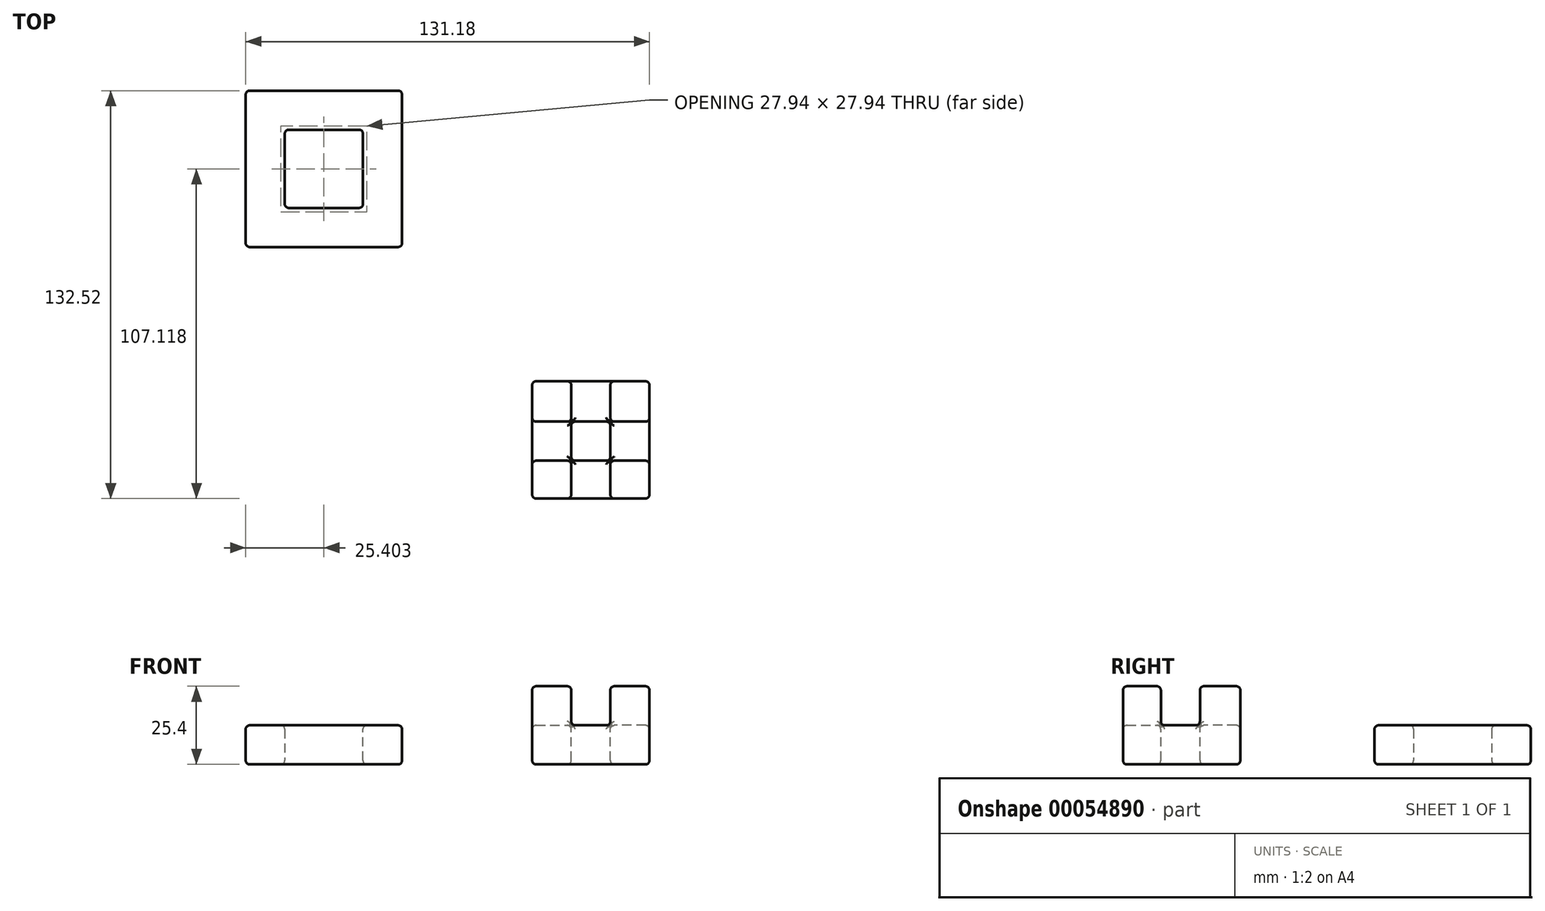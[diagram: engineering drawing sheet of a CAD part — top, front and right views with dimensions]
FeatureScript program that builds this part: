
annotation { "Feature Type Name" : "Feature", "Feature Type Description" : "" }
export const myFeature = defineFeature(function(context is Context, id is Id, definition is map)
    precondition{}
    {
        {
            var Q0;
            Q0=qCreatedBy(makeId("Top.planeOp"),FACE);
            var sketch = newSketch(context, id + "F0", { "sketchPlane" : qUnion([Q0])});
            skLineSegment(sketch, "E0.bottom", {"start": v(-78.93, 70.47) * mm, "end": v(-66.23, 70.47) * mm});
            skLineSegment(sketch, "E0.top", {"start": v(-78.93, 19.67) * mm, "end": v(-66.23, 19.67) * mm});
            skLineSegment(sketch, "E0.left", {"start": v(-78.93, 70.47) * mm, "end": v(-78.93, 19.67) * mm});
            skLineSegment(sketch, "E0.right", {"start": v(-66.23, 70.47) * mm, "end": v(-66.23, 19.67) * mm});
            skLineSegment(sketch, "E1.bottom", {"start": v(-78.93, 19.67) * mm, "end": v(-40.83, 19.67) * mm});
            skLineSegment(sketch, "E1.top", {"start": v(-78.93, 32.37) * mm, "end": v(-40.83, 32.37) * mm});
            skLineSegment(sketch, "E1.left", {"start": v(-78.93, 19.67) * mm, "end": v(-78.93, 32.37) * mm});
            skLineSegment(sketch, "E1.right", {"start": v(-40.83, 19.67) * mm, "end": v(-40.83, 32.37) * mm});
            skLineSegment(sketch, "E2.bottom", {"start": v(-28.13, 19.67) * mm, "end": v(-40.83, 19.67) * mm});
            skLineSegment(sketch, "E2.top", {"start": v(-28.13, 70.47) * mm, "end": v(-40.83, 70.47) * mm});
            skLineSegment(sketch, "E2.left", {"start": v(-40.83, 19.67) * mm, "end": v(-40.83, 70.47) * mm});
            skLineSegment(sketch, "E2.right", {"start": v(-28.13, 19.67) * mm, "end": v(-28.13, 70.47) * mm});
            skSolve(sketch);
        }
        {
            var Q0;
            Q0 = qSketchRegion(id + "F0", true);
            extrude(context, id + "F1", {"entities" : qUnion([Q0]), "depth" : 12.7 * mm});
        }
        {
            var Q0;
            Q0=makeQuery(id+"F1.opExtrude","CAP_FACE",FACE,{"disambiguationData":[OSD([sQuery(id+"F0.wireOp",EDGE,"E0.bottom"),sQuery(id+"F0.wireOp",EDGE,"E0.left"),sQuery(id+"F0.wireOp",EDGE,"E0.right"),sQuery(id+"F0.wireOp",EDGE,"E1.bottom"),sQuery(id+"F0.wireOp",EDGE,"E1.top"),sQuery(id+"F0.wireOp",EDGE,"E1.left"),sQuery(id+"F0.wireOp",EDGE,"E2.bottom"),sQuery(id+"F0.wireOp",EDGE,"E2.top"),sQuery(id+"F0.wireOp",EDGE,"E2.left"),sQuery(id+"F0.wireOp",EDGE,"E2.right")])],"isStart":false});
            var sketch = newSketch(context, id + "F2", { "sketchPlane" : qUnion([Q0])});
            skLineSegment(sketch, "E3.bottom", {"start": v(-78.93, 70.47) * mm, "end": v(-28.13, 70.47) * mm});
            skLineSegment(sketch, "E3.top", {"start": v(-78.93, 57.77) * mm, "end": v(-28.13, 57.77) * mm});
            skLineSegment(sketch, "E3.left", {"start": v(-78.93, 70.47) * mm, "end": v(-78.93, 57.77) * mm});
            skLineSegment(sketch, "E3.right", {"start": v(-28.13, 70.47) * mm, "end": v(-28.13, 57.77) * mm});
            skSolve(sketch);
        }
        {
            var Q0;
            Q0 = qSketchRegion(id + "F2", true);
            extrude(context, id + "F3", {"entities" : qUnion([Q0]), "operationType" : NewBodyOperationType.ADD, "oppositeDirection" : true, "depth" : 12.7 * mm});
        }
        {
            var Q0;
            Q0=qCreatedBy(makeId("Top.planeOp"),FACE);
            var sketch = newSketch(context, id + "F4", { "sketchPlane" : qUnion([Q0])});
            skLineSegment(sketch, "E4.rect.bottom", {"start": v(14.15, -23.95) * mm, "end": v(52.25, -23.95) * mm});
            skLineSegment(sketch, "E4.rect.top", {"start": v(14.15, -62.05) * mm, "end": v(52.25, -62.05) * mm});
            skLineSegment(sketch, "E4.rect.left", {"start": v(14.15, -23.95) * mm, "end": v(14.15, -62.05) * mm});
            skLineSegment(sketch, "E4.rect.right", {"start": v(52.25, -23.95) * mm, "end": v(52.25, -62.05) * mm});
            skPoint(sketch, "E4.rect.middle", {"position": v(33.2, -43) * mm});
            skSolve(sketch);
        }
        {
            var Q0;
            Q0 = qSketchRegion(id + "F4", true);
            extrude(context, id + "F5", {"entities" : qUnion([Q0]), "depth" : 12.7 * mm});
        }
        {
            var Q0;
            Q0=makeQuery(id+"F5.opExtrude","CAP_FACE",FACE,{"disambiguationData":[OSD([sQuery(id+"F4.wireOp",EDGE,"E4.rect.bottom"),sQuery(id+"F4.wireOp",EDGE,"E4.rect.top"),sQuery(id+"F4.wireOp",EDGE,"E4.rect.left"),sQuery(id+"F4.wireOp",EDGE,"E4.rect.right")])],"isStart":false});
            var sketch = newSketch(context, id + "F6", { "sketchPlane" : qUnion([Q0])});
            skLineSegment(sketch, "E5.bottom", {"start": v(14.15, -23.95) * mm, "end": v(26.85, -23.95) * mm});
            skLineSegment(sketch, "E5.top", {"start": v(14.15, -37.07) * mm, "end": v(26.85, -37.07) * mm});
            skLineSegment(sketch, "E5.left", {"start": v(14.15, -23.95) * mm, "end": v(14.15, -37.07) * mm});
            skLineSegment(sketch, "E5.right", {"start": v(26.85, -23.95) * mm, "end": v(26.85, -37.07) * mm});
            skLineSegment(sketch, "E6.bottom", {"start": v(52.25, -23.95) * mm, "end": v(39.55, -23.95) * mm});
            skLineSegment(sketch, "E6.top", {"start": v(52.25, -37.07) * mm, "end": v(39.55, -37.07) * mm});
            skLineSegment(sketch, "E6.left", {"start": v(52.25, -23.95) * mm, "end": v(52.25, -37.07) * mm});
            skLineSegment(sketch, "E6.right", {"start": v(39.55, -23.95) * mm, "end": v(39.55, -37.07) * mm});
            skLineSegment(sketch, "E7.bottom", {"start": v(52.25, -62.05) * mm, "end": v(39.55, -62.05) * mm});
            skLineSegment(sketch, "E7.top", {"start": v(52.25, -49.77) * mm, "end": v(39.55, -49.77) * mm});
            skLineSegment(sketch, "E7.left", {"start": v(52.25, -62.05) * mm, "end": v(52.25, -49.77) * mm});
            skLineSegment(sketch, "E7.right", {"start": v(39.55, -62.05) * mm, "end": v(39.55, -49.77) * mm});
            skLineSegment(sketch, "E8.bottom", {"start": v(14.15, -62.05) * mm, "end": v(26.85, -62.05) * mm});
            skLineSegment(sketch, "E8.top", {"start": v(14.15, -49.77) * mm, "end": v(26.85, -49.77) * mm});
            skLineSegment(sketch, "E8.left", {"start": v(14.15, -62.05) * mm, "end": v(14.15, -49.77) * mm});
            skLineSegment(sketch, "E8.right", {"start": v(26.85, -62.05) * mm, "end": v(26.85, -49.77) * mm});
            skSolve(sketch);
        }
        {
            var Q0;
            Q0 = qSketchRegion(id + "F6", true);
            extrude(context, id + "F7", {"entities" : qUnion([Q0]), "operationType" : NewBodyOperationType.ADD, "depth" : 12.7 * mm});
        }
        {
            var Q0;
            Q0=makeQuery(id+"F7.opExtrude","CAP_FACE",FACE,{"disambiguationData":[OSD([sQuery(id+"F6.wireOp",EDGE,"E5.bottom"),sQuery(id+"F6.wireOp",EDGE,"E5.top"),sQuery(id+"F6.wireOp",EDGE,"E5.left"),sQuery(id+"F6.wireOp",EDGE,"E5.right")])],"isStart":false});
            var sketch = newSketch(context, id + "F8", { "sketchPlane" : qUnion([Q0])});
            skLineSegment(sketch, "E9.bottom", {"start": v(26.85, -37.07) * mm, "end": v(39.55, -37.07) * mm});
            skLineSegment(sketch, "E9.top", {"start": v(26.85, -49.77) * mm, "end": v(39.55, -49.77) * mm});
            skLineSegment(sketch, "E9.left", {"start": v(26.85, -37.07) * mm, "end": v(26.85, -49.77) * mm});
            skLineSegment(sketch, "E9.right", {"start": v(39.55, -37.07) * mm, "end": v(39.55, -49.77) * mm});
            skSolve(sketch);
        }
        {
            var Q0;
            Q0 = qSketchRegion(id + "F8", true);
            extrude(context, id + "F9", {"entities" : qUnion([Q0]), "operationType" : NewBodyOperationType.REMOVE, "oppositeDirection" : true, "depth" : 25.4 * mm});
        }
        {
            var Q0;
            Q0=makeQuery(id+"F7.opExtrude","CAP_FACE",FACE,{"disambiguationData":[OSD([sQuery(id+"F6.wireOp",EDGE,"E5.bottom"),sQuery(id+"F6.wireOp",EDGE,"E5.top"),sQuery(id+"F6.wireOp",EDGE,"E5.left"),sQuery(id+"F6.wireOp",EDGE,"E5.right")])],"isStart":false});
            var Q1;
            Q1=makeQuery(id+"F7.boolean.opBoolean","MERGE",FACE,{"derivedFrom":[makeQuery(id+"F5.opExtrude","SWEPT_FACE",FACE,{"disambiguationData":[OSD([sQuery(id+"F4.wireOp",EDGE,"E4.rect.bottom")])]}),makeQuery(id+"F7.opExtrude","SWEPT_FACE",FACE,{"disambiguationData":[OSD([sQuery(id+"F6.wireOp",EDGE,"E5.bottom")])]}),makeQuery(id+"F7.opExtrude","SWEPT_FACE",FACE,{"disambiguationData":[OSD([sQuery(id+"F6.wireOp",EDGE,"E6.bottom")])]})]});
            var Q2;
            Q2=makeQuery(id+"F9.boolean.opBoolean","COPY",FACE,{"derivedFrom":makeQuery(id+"F9.opExtrude","SWEPT_FACE",FACE,{"disambiguationData":[OSD([sQuery(id+"F8.wireOp",EDGE,"E9.top")])]})});
            var Q3;
            Q3=makeQuery(id+"F7.opExtrude","SWEPT_FACE",FACE,{"disambiguationData":[OSD([sQuery(id+"F6.wireOp",EDGE,"E8.right")])]});
            var Q4;
            Q4=makeQuery(id+"F7.opExtrude","SWEPT_FACE",FACE,{"disambiguationData":[OSD([sQuery(id+"F6.wireOp",EDGE,"E5.top")])]});
            var Q5;
            Q5=makeQuery(id+"F7.boolean.opBoolean","MERGE",FACE,{"derivedFrom":[makeQuery(id+"F5.opExtrude","SWEPT_FACE",FACE,{"disambiguationData":[OSD([sQuery(id+"F4.wireOp",EDGE,"E4.rect.top")])]}),makeQuery(id+"F7.opExtrude","SWEPT_FACE",FACE,{"disambiguationData":[OSD([sQuery(id+"F6.wireOp",EDGE,"E7.bottom")])]}),makeQuery(id+"F7.opExtrude","SWEPT_FACE",FACE,{"disambiguationData":[OSD([sQuery(id+"F6.wireOp",EDGE,"E8.bottom")])]})]});
            var Q6;
            Q6=makeQuery(id+"F7.opExtrude","CAP_FACE",FACE,{"disambiguationData":[OSD([sQuery(id+"F6.wireOp",EDGE,"E6.bottom"),sQuery(id+"F6.wireOp",EDGE,"E6.top"),sQuery(id+"F6.wireOp",EDGE,"E6.left"),sQuery(id+"F6.wireOp",EDGE,"E6.right")])],"isStart":false});
            var Q7;
            Q7=makeQuery(id+"F7.boolean.opBoolean","MERGE",FACE,{"derivedFrom":[makeQuery(id+"F5.opExtrude","SWEPT_FACE",FACE,{"disambiguationData":[OSD([sQuery(id+"F4.wireOp",EDGE,"E4.rect.left")])]}),makeQuery(id+"F7.opExtrude","SWEPT_FACE",FACE,{"disambiguationData":[OSD([sQuery(id+"F6.wireOp",EDGE,"E5.left")])]}),makeQuery(id+"F7.opExtrude","SWEPT_FACE",FACE,{"disambiguationData":[OSD([sQuery(id+"F6.wireOp",EDGE,"E8.left")])]})]});
            var Q8;
            Q8=makeQuery(id+"F7.boolean.opBoolean","MERGE",FACE,{"derivedFrom":[makeQuery(id+"F5.opExtrude","SWEPT_FACE",FACE,{"disambiguationData":[OSD([sQuery(id+"F4.wireOp",EDGE,"E4.rect.right")])]}),makeQuery(id+"F7.opExtrude","SWEPT_FACE",FACE,{"disambiguationData":[OSD([sQuery(id+"F6.wireOp",EDGE,"E6.left")])]}),makeQuery(id+"F7.opExtrude","SWEPT_FACE",FACE,{"disambiguationData":[OSD([sQuery(id+"F6.wireOp",EDGE,"E7.left")])]})]});
            var Q9;
            Q9=makeQuery(id+"F5.opExtrude","CAP_EDGE",EDGE,{"disambiguationData":[OSD([sQuery(id+"F4.wireOp",EDGE,"E4.rect.bottom")])],"isStart":false});
            var Q10;
            Q10=makeQuery(id+"F7.opExtrude","SWEPT_FACE",FACE,{"disambiguationData":[OSD([sQuery(id+"F6.wireOp",EDGE,"E6.right")])]});
            var Q11;
            Q11=makeQuery(id+"F5.opExtrude","CAP_EDGE",EDGE,{"disambiguationData":[OSD([sQuery(id+"F4.wireOp",EDGE,"E4.rect.right")])],"isStart":false});
            var Q12;
            Q12=makeQuery(id+"F7.opExtrude","SWEPT_FACE",FACE,{"disambiguationData":[OSD([sQuery(id+"F6.wireOp",EDGE,"E8.top")])]});
            var Q13;
            Q13=makeQuery(id+"F7.opExtrude","SWEPT_FACE",FACE,{"disambiguationData":[OSD([sQuery(id+"F6.wireOp",EDGE,"E7.right")])]});
            var Q14;
            Q14=makeQuery(id+"F7.opExtrude","CAP_FACE",FACE,{"disambiguationData":[OSD([sQuery(id+"F6.wireOp",EDGE,"E8.bottom"),sQuery(id+"F6.wireOp",EDGE,"E8.top"),sQuery(id+"F6.wireOp",EDGE,"E8.left"),sQuery(id+"F6.wireOp",EDGE,"E8.right")])],"isStart":false});
            var Q15;
            Q15=makeQuery(id+"F7.opExtrude","SWEPT_FACE",FACE,{"disambiguationData":[OSD([sQuery(id+"F6.wireOp",EDGE,"E7.top")])]});
            var Q16;
            Q16=makeQuery(id+"F7.opExtrude","CAP_FACE",FACE,{"disambiguationData":[OSD([sQuery(id+"F6.wireOp",EDGE,"E7.bottom"),sQuery(id+"F6.wireOp",EDGE,"E7.top"),sQuery(id+"F6.wireOp",EDGE,"E7.left"),sQuery(id+"F6.wireOp",EDGE,"E7.right")])],"isStart":false});
            var Q17;
            Q17=makeQuery(id+"F9.boolean.opBoolean","COPY",FACE,{"derivedFrom":makeQuery(id+"F9.opExtrude","SWEPT_FACE",FACE,{"disambiguationData":[OSD([sQuery(id+"F8.wireOp",EDGE,"E9.left")])]})});
            var Q18;
            {var subQ0=sQuery(id+"F4.wireOp",EDGE,"E4.rect.bottom");var subQ1=makeQuery(id+"F5.opExtrude","CAP_FACE",FACE,{"disambiguationData":[OSD([subQ0,sQuery(id+"F4.wireOp",EDGE,"E4.rect.top"),sQuery(id+"F4.wireOp",EDGE,"E4.rect.left"),sQuery(id+"F4.wireOp",EDGE,"E4.rect.right")])],"isStart":false});Q18=makeQuery(id+"F9.boolean.opBoolean","SPLIT",FACE,{"disambiguationData":[TD([makeQuery(id+"F5.opExtrude","SWEPT_FACE",FACE,{"disambiguationData":[OSD([subQ0])]})])],"derivedFrom":subQ1});}
            var Q19;
            {var subQ0=sQuery(id+"F4.wireOp",EDGE,"E4.rect.top");var subQ1=makeQuery(id+"F5.opExtrude","CAP_FACE",FACE,{"disambiguationData":[OSD([sQuery(id+"F4.wireOp",EDGE,"E4.rect.bottom"),subQ0,sQuery(id+"F4.wireOp",EDGE,"E4.rect.left"),sQuery(id+"F4.wireOp",EDGE,"E4.rect.right")])],"isStart":false});Q19=makeQuery(id+"F9.boolean.opBoolean","SPLIT",FACE,{"disambiguationData":[TD([makeQuery(id+"F5.opExtrude","SWEPT_FACE",FACE,{"disambiguationData":[OSD([subQ0])]})])],"derivedFrom":subQ1});}
            var Q20;
            {var subQ0=sQuery(id+"F4.wireOp",EDGE,"E4.rect.left");var subQ1=makeQuery(id+"F5.opExtrude","CAP_FACE",FACE,{"disambiguationData":[OSD([sQuery(id+"F4.wireOp",EDGE,"E4.rect.bottom"),sQuery(id+"F4.wireOp",EDGE,"E4.rect.top"),subQ0,sQuery(id+"F4.wireOp",EDGE,"E4.rect.right")])],"isStart":false});Q20=makeQuery(id+"F9.boolean.opBoolean","SPLIT",FACE,{"disambiguationData":[TD([makeQuery(id+"F5.opExtrude","SWEPT_FACE",FACE,{"disambiguationData":[OSD([subQ0])]})])],"derivedFrom":subQ1});}
            var Q21;
            Q21=makeQuery(id+"F9.boolean.opBoolean","INTERSECT",EDGE,{"derivedFrom":[makeQuery(id+"F5.opExtrude","CAP_FACE",FACE,{"disambiguationData":[OSD([sQuery(id+"F4.wireOp",EDGE,"E4.rect.bottom"),sQuery(id+"F4.wireOp",EDGE,"E4.rect.top"),sQuery(id+"F4.wireOp",EDGE,"E4.rect.left"),sQuery(id+"F4.wireOp",EDGE,"E4.rect.right")])],"isStart":false}),makeQuery(id+"F9.opExtrude","SWEPT_FACE",FACE,{"disambiguationData":[OSD([sQuery(id+"F8.wireOp",EDGE,"E9.bottom")])]})]});
            var Q22;
            {var subQ0=sQuery(id+"F4.wireOp",EDGE,"E4.rect.right");var subQ1=makeQuery(id+"F5.opExtrude","CAP_FACE",FACE,{"disambiguationData":[OSD([sQuery(id+"F4.wireOp",EDGE,"E4.rect.bottom"),sQuery(id+"F4.wireOp",EDGE,"E4.rect.top"),sQuery(id+"F4.wireOp",EDGE,"E4.rect.left"),subQ0])],"isStart":false});Q22=makeQuery(id+"F9.boolean.opBoolean","SPLIT",FACE,{"disambiguationData":[TD([makeQuery(id+"F5.opExtrude","SWEPT_FACE",FACE,{"disambiguationData":[OSD([subQ0])]})])],"derivedFrom":subQ1});}
            var Q23;
            Q23=makeQuery(id+"F9.boolean.opBoolean","INTERSECT",EDGE,{"derivedFrom":[makeQuery(id+"F5.opExtrude","CAP_FACE",FACE,{"disambiguationData":[OSD([sQuery(id+"F4.wireOp",EDGE,"E4.rect.bottom"),sQuery(id+"F4.wireOp",EDGE,"E4.rect.top"),sQuery(id+"F4.wireOp",EDGE,"E4.rect.left"),sQuery(id+"F4.wireOp",EDGE,"E4.rect.right")])],"isStart":false}),makeQuery(id+"F9.opExtrude","SWEPT_FACE",FACE,{"disambiguationData":[OSD([sQuery(id+"F8.wireOp",EDGE,"E9.right")])]})]});
            var Q24;
            Q24=makeQuery(id+"F5.opExtrude","CAP_EDGE",EDGE,{"disambiguationData":[OSD([sQuery(id+"F4.wireOp",EDGE,"E4.rect.right")])],"isStart":true});
            var Q25;
            Q25=makeQuery(id+"F7.opExtrude","SWEPT_FACE",FACE,{"disambiguationData":[OSD([sQuery(id+"F6.wireOp",EDGE,"E5.right")])]});
            var Q26;
            Q26=makeQuery(id+"F5.opExtrude","CAP_EDGE",EDGE,{"disambiguationData":[OSD([sQuery(id+"F4.wireOp",EDGE,"E4.rect.bottom")])],"isStart":true});
            var Q27;
            Q27=makeQuery(id+"F7.opExtrude","SWEPT_FACE",FACE,{"disambiguationData":[OSD([sQuery(id+"F6.wireOp",EDGE,"E6.top")])]});
            var Q28;
            Q28=makeQuery(id+"F7.opExtrude","CAP_EDGE",EDGE,{"disambiguationData":[OSD([sQuery(id+"F6.wireOp",EDGE,"E7.right")])],"isStart":false});
            var Q29;
            Q29=makeQuery(id+"F5.opExtrude","CAP_EDGE",EDGE,{"disambiguationData":[OSD([sQuery(id+"F4.wireOp",EDGE,"E4.rect.top")])],"isStart":false});
            var Q30;
            Q30=makeQuery(id+"F5.opExtrude","CAP_EDGE",EDGE,{"disambiguationData":[OSD([sQuery(id+"F4.wireOp",EDGE,"E4.rect.left")])],"isStart":false});
            var Q31;
            Q31=makeQuery(id+"F9.boolean.opBoolean","COPY",FACE,{"derivedFrom":makeQuery(id+"F9.opExtrude","SWEPT_FACE",FACE,{"disambiguationData":[OSD([sQuery(id+"F8.wireOp",EDGE,"E9.bottom")])]})});
            var Q32;
            Q32=makeQuery(id+"F7.opExtrude","CAP_EDGE",EDGE,{"disambiguationData":[OSD([sQuery(id+"F6.wireOp",EDGE,"E5.bottom")])],"isStart":false});
            var Q33;
            Q33=makeQuery(id+"F7.opExtrude","CAP_EDGE",EDGE,{"disambiguationData":[OSD([sQuery(id+"F6.wireOp",EDGE,"E7.bottom")])],"isStart":false});
            var Q34;
            Q34=makeQuery(id+"F7.opExtrude","CAP_EDGE",EDGE,{"disambiguationData":[OSD([sQuery(id+"F6.wireOp",EDGE,"E5.left")])],"isStart":false});
            var Q35;
            Q35=makeQuery(id+"F7.opExtrude","CAP_EDGE",EDGE,{"disambiguationData":[OSD([sQuery(id+"F6.wireOp",EDGE,"E7.left")])],"isStart":false});
            var Q36;
            Q36=makeQuery(id+"F7.opExtrude","CAP_EDGE",EDGE,{"disambiguationData":[OSD([sQuery(id+"F6.wireOp",EDGE,"E5.top")])],"isStart":false});
            var Q37;
            Q37=makeQuery(id+"F7.opExtrude","CAP_EDGE",EDGE,{"disambiguationData":[OSD([sQuery(id+"F6.wireOp",EDGE,"E7.top")])],"isStart":false});
            var Q38;
            Q38=makeQuery(id+"F7.opExtrude","CAP_EDGE",EDGE,{"disambiguationData":[OSD([sQuery(id+"F6.wireOp",EDGE,"E8.top")])],"isStart":false});
            var Q39;
            Q39=makeQuery(id+"F7.opExtrude","CAP_EDGE",EDGE,{"disambiguationData":[OSD([sQuery(id+"F6.wireOp",EDGE,"E8.bottom")])],"isStart":false});
            var Q40;
            Q40=makeQuery(id+"F7.opExtrude","CAP_EDGE",EDGE,{"disambiguationData":[OSD([sQuery(id+"F6.wireOp",EDGE,"E6.bottom")])],"isStart":false});
            var Q41;
            Q41=makeQuery(id+"F7.opExtrude","CAP_EDGE",EDGE,{"disambiguationData":[OSD([sQuery(id+"F6.wireOp",EDGE,"E8.right")])],"isStart":false});
            var Q42;
            Q42=makeQuery(id+"F7.opExtrude","CAP_EDGE",EDGE,{"disambiguationData":[OSD([sQuery(id+"F6.wireOp",EDGE,"E6.right")])],"isStart":false});
            var Q43;
            Q43=makeQuery(id+"F7.opExtrude","CAP_EDGE",EDGE,{"disambiguationData":[OSD([sQuery(id+"F6.wireOp",EDGE,"E8.left")])],"isStart":false});
            var Q44;
            Q44=makeQuery(id+"F7.opExtrude","CAP_EDGE",EDGE,{"disambiguationData":[OSD([sQuery(id+"F6.wireOp",EDGE,"E6.left")])],"isStart":false});
            var Q45;
            Q45=makeQuery(id+"F9.boolean.opBoolean","COPY",FACE,{"derivedFrom":makeQuery(id+"F9.opExtrude","SWEPT_FACE",FACE,{"disambiguationData":[OSD([sQuery(id+"F8.wireOp",EDGE,"E9.right")])]})});
            var Q46;
            Q46=makeQuery(id+"F5.opExtrude","CAP_FACE",FACE,{"disambiguationData":[OSD([sQuery(id+"F4.wireOp",EDGE,"E4.rect.bottom"),sQuery(id+"F4.wireOp",EDGE,"E4.rect.top"),sQuery(id+"F4.wireOp",EDGE,"E4.rect.left"),sQuery(id+"F4.wireOp",EDGE,"E4.rect.right")])],"isStart":true});
            var Q47;
            Q47=makeQuery(id+"F9.boolean.opBoolean","INTERSECT",EDGE,{"derivedFrom":[makeQuery(id+"F5.opExtrude","CAP_FACE",FACE,{"disambiguationData":[OSD([sQuery(id+"F4.wireOp",EDGE,"E4.rect.bottom"),sQuery(id+"F4.wireOp",EDGE,"E4.rect.top"),sQuery(id+"F4.wireOp",EDGE,"E4.rect.left"),sQuery(id+"F4.wireOp",EDGE,"E4.rect.right")])],"isStart":false}),makeQuery(id+"F9.opExtrude","SWEPT_FACE",FACE,{"disambiguationData":[OSD([sQuery(id+"F8.wireOp",EDGE,"E9.left")])]})]});
            var Q48;
            Q48=makeQuery(id+"F9.boolean.opBoolean","INTERSECT",EDGE,{"derivedFrom":[makeQuery(id+"F5.opExtrude","CAP_FACE",FACE,{"disambiguationData":[OSD([sQuery(id+"F4.wireOp",EDGE,"E4.rect.bottom"),sQuery(id+"F4.wireOp",EDGE,"E4.rect.top"),sQuery(id+"F4.wireOp",EDGE,"E4.rect.left"),sQuery(id+"F4.wireOp",EDGE,"E4.rect.right")])],"isStart":false}),makeQuery(id+"F9.opExtrude","SWEPT_FACE",FACE,{"disambiguationData":[OSD([sQuery(id+"F8.wireOp",EDGE,"E9.top")])]})]});
            var Q49;
            Q49=makeQuery(id+"F5.opExtrude","CAP_EDGE",EDGE,{"disambiguationData":[OSD([sQuery(id+"F4.wireOp",EDGE,"E4.rect.left")])],"isStart":true});
            var Q50;
            Q50=makeQuery(id+"F7.opExtrude","CAP_EDGE",EDGE,{"disambiguationData":[OSD([sQuery(id+"F6.wireOp",EDGE,"E8.right")])],"isStart":true});
            var Q51;
            Q51=makeQuery(id+"F7.opExtrude","CAP_EDGE",EDGE,{"disambiguationData":[OSD([sQuery(id+"F6.wireOp",EDGE,"E8.top")])],"isStart":true});
            var Q52;
            Q52=makeQuery(id+"F7.opExtrude","CAP_EDGE",EDGE,{"disambiguationData":[OSD([sQuery(id+"F6.wireOp",EDGE,"E7.right")])],"isStart":true});
            var Q53;
            Q53=makeQuery(id+"F5.opExtrude","CAP_EDGE",EDGE,{"disambiguationData":[OSD([sQuery(id+"F4.wireOp",EDGE,"E4.rect.top")])],"isStart":true});
            var Q54;
            Q54=makeQuery(id+"F7.opExtrude","CAP_EDGE",EDGE,{"disambiguationData":[OSD([sQuery(id+"F6.wireOp",EDGE,"E5.right")])],"isStart":false});
            var Q55;
            Q55=makeQuery(id+"F7.opExtrude","CAP_EDGE",EDGE,{"disambiguationData":[OSD([sQuery(id+"F6.wireOp",EDGE,"E5.top")])],"isStart":true});
            var Q56;
            Q56=makeQuery(id+"F7.opExtrude","CAP_EDGE",EDGE,{"disambiguationData":[OSD([sQuery(id+"F6.wireOp",EDGE,"E6.right")])],"isStart":true});
            var Q57;
            Q57=makeQuery(id+"F7.opExtrude","CAP_EDGE",EDGE,{"disambiguationData":[OSD([sQuery(id+"F6.wireOp",EDGE,"E7.top")])],"isStart":true});
            var Q58;
            Q58=makeQuery(id+"F7.opExtrude","CAP_EDGE",EDGE,{"disambiguationData":[OSD([sQuery(id+"F6.wireOp",EDGE,"E6.top")])],"isStart":false});
            var Q59;
            Q59=makeQuery(id+"F9.boolean.opBoolean","COPY",EDGE,{"derivedFrom":makeQuery(id+"F9.opExtrude","CAP_EDGE",EDGE,{"disambiguationData":[OSD([sQuery(id+"F8.wireOp",EDGE,"E9.bottom")])],"isStart":false})});
            var Q60;
            Q60=makeQuery(id+"F9.boolean.opBoolean","COPY",EDGE,{"derivedFrom":makeQuery(id+"F9.opExtrude","CAP_EDGE",EDGE,{"disambiguationData":[OSD([sQuery(id+"F8.wireOp",EDGE,"E9.top")])],"isStart":false})});
            var Q61;
            Q61=makeQuery(id+"F9.boolean.opBoolean","COPY",EDGE,{"derivedFrom":makeQuery(id+"F9.opExtrude","CAP_EDGE",EDGE,{"disambiguationData":[OSD([sQuery(id+"F8.wireOp",EDGE,"E9.left")])],"isStart":false})});
            var Q62;
            Q62=makeQuery(id+"F9.boolean.opBoolean","COPY",EDGE,{"derivedFrom":makeQuery(id+"F9.opExtrude","CAP_EDGE",EDGE,{"disambiguationData":[OSD([sQuery(id+"F8.wireOp",EDGE,"E9.right")])],"isStart":false})});
            var Q63;
            Q63=makeQuery(id+"F7.opExtrude","CAP_EDGE",EDGE,{"disambiguationData":[OSD([sQuery(id+"F6.wireOp",EDGE,"E5.right")])],"isStart":true});
            var Q64;
            Q64=makeQuery(id+"F7.opExtrude","CAP_EDGE",EDGE,{"disambiguationData":[OSD([sQuery(id+"F6.wireOp",EDGE,"E6.top")])],"isStart":true});
            fillet(context, id + "F10", {"entities" : qUnion([Q0, Q1, Q2, Q3, Q4, Q5, Q6, Q7, Q8, Q9, Q10, Q11, Q12, Q13, Q14, Q15, Q16, Q17, Q18, Q19, Q20, Q21, Q22, Q23, Q24, Q25, Q26, Q27, Q28, Q29, Q30, Q31, Q32, Q33, Q34, Q35, Q36, Q37, Q38, Q39, Q40, Q41, Q42, Q43, Q44, Q45, Q46, Q47, Q48, Q49, Q50, Q51, Q52, Q53, Q54, Q55, Q56, Q57, Q58, Q59, Q60, Q61, Q62, Q63, Q64]), "radius" : 1.27 * mm, "tangentPropagation" : true, "allowEdgeOverflow" : false});
        }
        {
            var Q0;
            Q0=makeQuery(id+"F3.boolean.opBoolean","MERGE",FACE,{"derivedFrom":[makeQuery(id+"F1.opExtrude","SWEPT_FACE",FACE,{"disambiguationData":[OSD([sQuery(id+"F0.wireOp",EDGE,"E0.bottom")])]}),makeQuery(id+"F1.opExtrude","SWEPT_FACE",FACE,{"disambiguationData":[OSD([sQuery(id+"F0.wireOp",EDGE,"E2.top")])]}),makeQuery(id+"F3.opExtrude","SWEPT_FACE",FACE,{"disambiguationData":[OSD([sQuery(id+"F2.wireOp",EDGE,"E3.bottom")])]})]});
            var Q1;
            Q1=makeQuery(id+"F3.boolean.opBoolean","MERGE",FACE,{"derivedFrom":[makeQuery(id+"F1.opExtrude","CAP_FACE",FACE,{"disambiguationData":[OSD([sQuery(id+"F0.wireOp",EDGE,"E0.bottom"),sQuery(id+"F0.wireOp",EDGE,"E0.left"),sQuery(id+"F0.wireOp",EDGE,"E0.right"),sQuery(id+"F0.wireOp",EDGE,"E1.bottom"),sQuery(id+"F0.wireOp",EDGE,"E1.top"),sQuery(id+"F0.wireOp",EDGE,"E1.left"),sQuery(id+"F0.wireOp",EDGE,"E2.bottom"),sQuery(id+"F0.wireOp",EDGE,"E2.top"),sQuery(id+"F0.wireOp",EDGE,"E2.left"),sQuery(id+"F0.wireOp",EDGE,"E2.right")])],"isStart":false}),makeQuery(id+"F3.opExtrude","CAP_FACE",FACE,{"disambiguationData":[OSD([sQuery(id+"F2.wireOp",EDGE,"E3.bottom"),sQuery(id+"F2.wireOp",EDGE,"E3.top"),sQuery(id+"F2.wireOp",EDGE,"E3.left"),sQuery(id+"F2.wireOp",EDGE,"E3.right")])],"isStart":true})]});
            var Q2;
            Q2=makeQuery(id+"F1.opExtrude","SWEPT_FACE",FACE,{"disambiguationData":[OSD([sQuery(id+"F0.wireOp",EDGE,"E0.left"),sQuery(id+"F0.wireOp",EDGE,"E1.left")])]});
            var Q3;
            Q3=makeQuery(id+"F1.opExtrude","CAP_EDGE",EDGE,{"disambiguationData":[OSD([sQuery(id+"F0.wireOp",EDGE,"E0.right")])],"isStart":false});
            var Q4;
            Q4=makeQuery(id+"F1.opExtrude","SWEPT_FACE",FACE,{"disambiguationData":[OSD([sQuery(id+"F0.wireOp",EDGE,"E2.right")])]});
            var Q5;
            Q5=makeQuery(id+"F3.opExtrude","SWEPT_FACE",FACE,{"disambiguationData":[OSD([sQuery(id+"F2.wireOp",EDGE,"E3.top")])]});
            var Q6;
            Q6=makeQuery(id+"F1.opExtrude","CAP_EDGE",EDGE,{"disambiguationData":[OSD([sQuery(id+"F0.wireOp",EDGE,"E2.left")])],"isStart":false});
            var Q7;
            Q7=makeQuery(id+"F1.opExtrude","SWEPT_FACE",FACE,{"disambiguationData":[OSD([sQuery(id+"F0.wireOp",EDGE,"E1.bottom"),sQuery(id+"F0.wireOp",EDGE,"E2.bottom")])]});
            var Q8;
            Q8=makeQuery(id+"F1.opExtrude","SWEPT_FACE",FACE,{"disambiguationData":[OSD([sQuery(id+"F0.wireOp",EDGE,"E1.top")])]});
            var Q9;
            Q9=makeQuery(id+"F3.boolean.opBoolean","MERGE",FACE,{"derivedFrom":[makeQuery(id+"F1.opExtrude","CAP_FACE",FACE,{"disambiguationData":[OSD([sQuery(id+"F0.wireOp",EDGE,"E0.bottom"),sQuery(id+"F0.wireOp",EDGE,"E0.left"),sQuery(id+"F0.wireOp",EDGE,"E0.right"),sQuery(id+"F0.wireOp",EDGE,"E1.bottom"),sQuery(id+"F0.wireOp",EDGE,"E1.top"),sQuery(id+"F0.wireOp",EDGE,"E1.left"),sQuery(id+"F0.wireOp",EDGE,"E2.bottom"),sQuery(id+"F0.wireOp",EDGE,"E2.top"),sQuery(id+"F0.wireOp",EDGE,"E2.left"),sQuery(id+"F0.wireOp",EDGE,"E2.right")])],"isStart":true}),makeQuery(id+"F3.opExtrude","CAP_FACE",FACE,{"disambiguationData":[OSD([sQuery(id+"F2.wireOp",EDGE,"E3.bottom"),sQuery(id+"F2.wireOp",EDGE,"E3.top"),sQuery(id+"F2.wireOp",EDGE,"E3.left"),sQuery(id+"F2.wireOp",EDGE,"E3.right")])],"isStart":false})]});
            var Q10;
            Q10=makeQuery(id+"F3.boolean.opBoolean","MERGE",EDGE,{"derivedFrom":[makeQuery(id+"F1.opExtrude","CAP_EDGE",EDGE,{"disambiguationData":[OSD([sQuery(id+"F0.wireOp",EDGE,"E0.bottom")])],"isStart":false}),makeQuery(id+"F1.opExtrude","CAP_EDGE",EDGE,{"disambiguationData":[OSD([sQuery(id+"F0.wireOp",EDGE,"E2.top")])],"isStart":false}),makeQuery(id+"F3.opExtrude","CAP_EDGE",EDGE,{"disambiguationData":[OSD([sQuery(id+"F2.wireOp",EDGE,"E3.bottom")])],"isStart":true})]});
            var Q11;
            Q11=makeQuery(id+"F1.opExtrude","CAP_EDGE",EDGE,{"disambiguationData":[OSD([sQuery(id+"F0.wireOp",EDGE,"E0.left"),sQuery(id+"F0.wireOp",EDGE,"E1.left")])],"isStart":false});
            var Q12;
            Q12=makeQuery(id+"F1.opExtrude","SWEPT_FACE",FACE,{"disambiguationData":[OSD([sQuery(id+"F0.wireOp",EDGE,"E0.right")])]});
            var Q13;
            Q13=makeQuery(id+"F1.opExtrude","SWEPT_FACE",FACE,{"disambiguationData":[OSD([sQuery(id+"F0.wireOp",EDGE,"E2.left")])]});
            var Q14;
            Q14=makeQuery(id+"F1.opExtrude","CAP_EDGE",EDGE,{"disambiguationData":[OSD([sQuery(id+"F0.wireOp",EDGE,"E2.right")])],"isStart":false});
            var Q15;
            Q15=makeQuery(id+"F3.opExtrude","CAP_EDGE",EDGE,{"disambiguationData":[OSD([sQuery(id+"F2.wireOp",EDGE,"E3.top")])],"isStart":true});
            var Q16;
            Q16=makeQuery(id+"F1.opExtrude","CAP_EDGE",EDGE,{"disambiguationData":[OSD([sQuery(id+"F0.wireOp",EDGE,"E1.bottom"),sQuery(id+"F0.wireOp",EDGE,"E2.bottom")])],"isStart":false});
            var Q17;
            Q17=makeQuery(id+"F1.opExtrude","CAP_EDGE",EDGE,{"disambiguationData":[OSD([sQuery(id+"F0.wireOp",EDGE,"E1.top")])],"isStart":false});
            var Q18;
            Q18=makeQuery(id+"F3.boolean.opBoolean","MERGE",EDGE,{"derivedFrom":[makeQuery(id+"F1.opExtrude","CAP_EDGE",EDGE,{"disambiguationData":[OSD([sQuery(id+"F0.wireOp",EDGE,"E0.bottom")])],"isStart":true}),makeQuery(id+"F1.opExtrude","CAP_EDGE",EDGE,{"disambiguationData":[OSD([sQuery(id+"F0.wireOp",EDGE,"E2.top")])],"isStart":true}),makeQuery(id+"F3.opExtrude","CAP_EDGE",EDGE,{"disambiguationData":[OSD([sQuery(id+"F2.wireOp",EDGE,"E3.bottom")])],"isStart":false})]});
            var Q19;
            Q19=makeQuery(id+"F1.opExtrude","CAP_EDGE",EDGE,{"disambiguationData":[OSD([sQuery(id+"F0.wireOp",EDGE,"E0.left"),sQuery(id+"F0.wireOp",EDGE,"E1.left")])],"isStart":true});
            var Q20;
            Q20=makeQuery(id+"F1.opExtrude","CAP_EDGE",EDGE,{"disambiguationData":[OSD([sQuery(id+"F0.wireOp",EDGE,"E0.right")])],"isStart":true});
            var Q21;
            Q21=makeQuery(id+"F1.opExtrude","CAP_EDGE",EDGE,{"disambiguationData":[OSD([sQuery(id+"F0.wireOp",EDGE,"E2.left")])],"isStart":true});
            var Q22;
            Q22=makeQuery(id+"F1.opExtrude","CAP_EDGE",EDGE,{"disambiguationData":[OSD([sQuery(id+"F0.wireOp",EDGE,"E2.right")])],"isStart":true});
            var Q23;
            Q23=makeQuery(id+"F3.opExtrude","CAP_EDGE",EDGE,{"disambiguationData":[OSD([sQuery(id+"F2.wireOp",EDGE,"E3.top")])],"isStart":false});
            var Q24;
            Q24=makeQuery(id+"F1.opExtrude","CAP_EDGE",EDGE,{"disambiguationData":[OSD([sQuery(id+"F0.wireOp",EDGE,"E1.top")])],"isStart":true});
            var Q25;
            Q25=makeQuery(id+"F1.opExtrude","CAP_EDGE",EDGE,{"disambiguationData":[OSD([sQuery(id+"F0.wireOp",EDGE,"E1.bottom"),sQuery(id+"F0.wireOp",EDGE,"E2.bottom")])],"isStart":true});
            fillet(context, id + "F11", {"entities" : qUnion([Q0, Q1, Q2, Q3, Q4, Q5, Q6, Q7, Q8, Q9, Q10, Q11, Q12, Q13, Q14, Q15, Q16, Q17, Q18, Q19, Q20, Q21, Q22, Q23, Q24, Q25]), "radius" : 1.27 * mm, "tangentPropagation" : true, "allowEdgeOverflow" : false});
        }
    });
